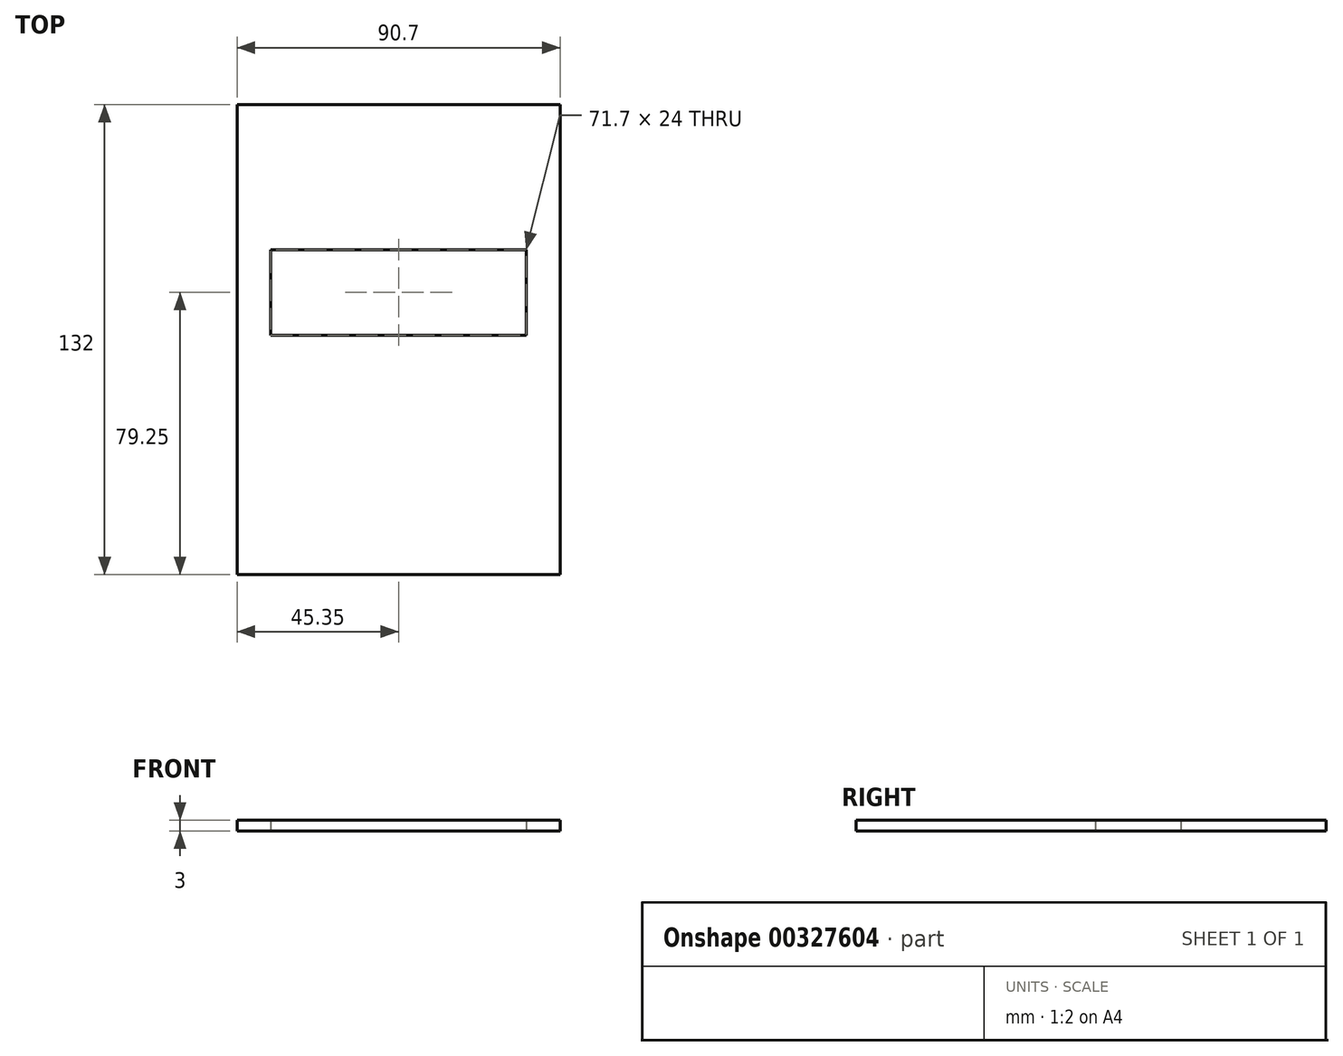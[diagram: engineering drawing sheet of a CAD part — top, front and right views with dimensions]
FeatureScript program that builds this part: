
annotation { "Feature Type Name" : "Feature", "Feature Type Description" : "" }
export const myFeature = defineFeature(function(context is Context, id is Id, definition is map)
    precondition{}
    {
        {
            var Q0;
            Q0=qCreatedBy(makeId("Top.planeOp"),FACE);
            var sketch = newSketch(context, id + "F0", { "sketchPlane" : qUnion([Q0])});
            skLineSegment(sketch, "E0.bottom", {"start": v(0, 116) * mm, "end": v(82.7, 116) * mm});
            skLineSegment(sketch, "E0.top", {"start": v(0, 0) * mm, "end": v(82.7, 0) * mm});
            skLineSegment(sketch, "E0.left", {"start": v(0, 116) * mm, "end": v(0, 0) * mm});
            skLineSegment(sketch, "E0.right", {"start": v(82.7, 116) * mm, "end": v(82.7, 0) * mm});
            skLineSegment(sketch, "E1.bottom", {"start": v(5.5, 84.25) * mm, "end": v(77.2, 84.25) * mm});
            skLineSegment(sketch, "E1.top", {"start": v(5.5, 60.25) * mm, "end": v(77.2, 60.25) * mm});
            skLineSegment(sketch, "E1.left", {"start": v(5.5, 84.25) * mm, "end": v(5.5, 60.25) * mm});
            skLineSegment(sketch, "E1.right", {"start": v(77.2, 84.25) * mm, "end": v(77.2, 60.25) * mm});
            skLineSegment(sketch, "E2.bottom", {"start": v(-4, 125) * mm, "end": v(86.7, 125) * mm});
            skLineSegment(sketch, "E2.top", {"start": v(-4, -7) * mm, "end": v(86.7, -7) * mm});
            skLineSegment(sketch, "E2.left", {"start": v(-4, 125) * mm, "end": v(-4, -7) * mm});
            skLineSegment(sketch, "E2.right", {"start": v(86.7, 125) * mm, "end": v(86.7, -7) * mm});
            skSolve(sketch);
        }
        {
            var Q0;
            Q0=makeQuery(id+"F0.imprint","IMPRINT",FACE,{"disambiguationData":[TD([[makeQuery(id+"F0.imprint","IMPRINT",EDGE,{"derivedFrom":sQuery(id+"F0.wireOp",EDGE,"E0.bottom")}),-1.0]])]});
            var Q1;
            Q1=makeQuery(id+"F0.imprint","IMPRINT",FACE,{"disambiguationData":[TD([[makeQuery(id+"F0.imprint","IMPRINT",EDGE,{"derivedFrom":sQuery(id+"F0.wireOp",EDGE,"E0.bottom")}),1.0]])]});
            extrude(context, id + "F1", {"entities" : qUnion([Q0, Q1]), "depth" : 3 * mm});
        }
    });
